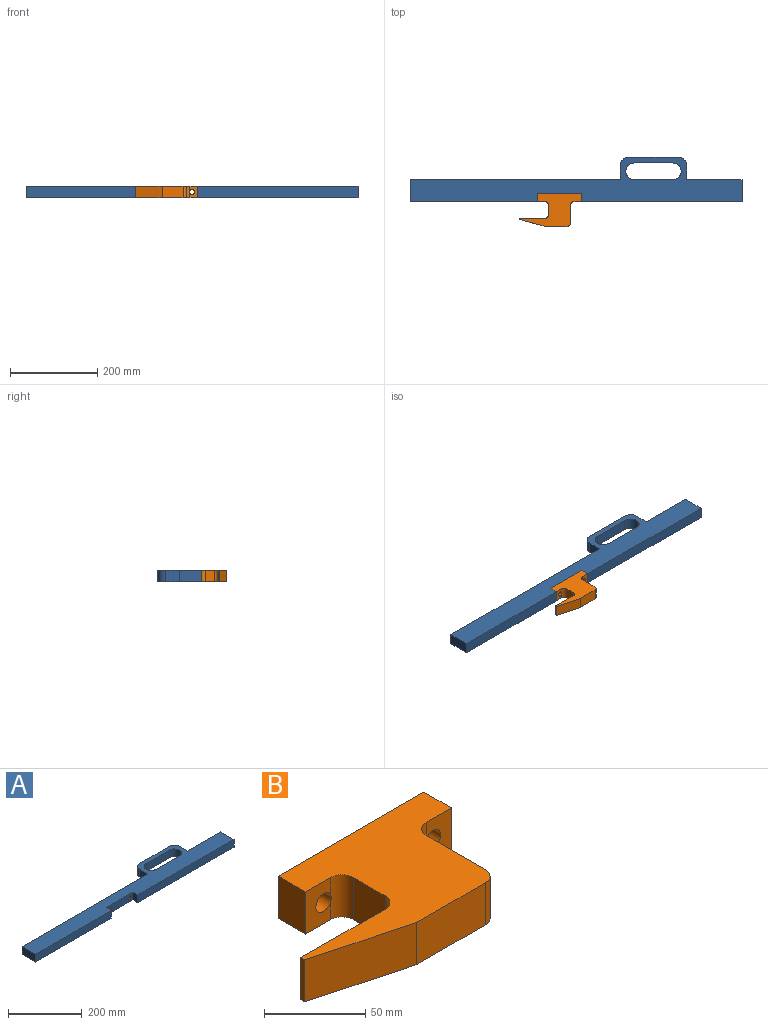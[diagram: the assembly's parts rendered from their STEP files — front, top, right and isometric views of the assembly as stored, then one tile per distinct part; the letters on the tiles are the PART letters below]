
ASSEMBLY  parts=2 mates=1
PART A: 34 faces, bbox 762x101.6x25.4 mm
  f0: plane 368.3x25.4mm, normal (0,-1,0), area 9354.8mm2, adj f1,f7,f14,f28
  f1: plane 762x101.6mm, normal (0,0,1), area 39833.1mm2, adj f0,f4,f5,f6,f7,f8,f9,f10
  f2: cylinder r=6.74mm len=19.05mm, axis (0,1,0), area 807.2mm2, adj f23,f29
  f3: cylinder r=6.74mm len=19.05mm, axis (0,1,0), area 807.2mm2, adj f25,f29
  f4: plane 88.9x25.4mm, normal (0,1,0), area 2258.1mm2, adj f1,f14,f32,f33
  f5: plane 88.9x25.4mm, normal (0,-1,0), area 2258.1mm2, adj f1,f14,f32,f33
  f6: plane 292.1x25.4mm, normal (0,-1,0), area 7419.3mm2, adj f1,f13,f14,f27
  f7: plane 50.8x25.4mm, normal (1,0,0), area 1290.3mm2, adj f0,f1,f8,f14
  f8: plane 127x25.4mm, normal (0,1,0), area 3225.8mm2, adj f1,f7,f9,f14
  f9: plane 31.75x25.4mm, normal (1,0,0), area 806.5mm2, adj f1,f8,f14,f30
  f10: plane 114.3x25.4mm, normal (0,1,0), area 2903.2mm2, adj f1,f14,f30,f31
  f11: plane 31.75x25.4mm, normal (-1,0,0), area 806.5mm2, adj f1,f12,f14,f31
  f12: plane 482.6x25.4mm, normal (0,1,0), area 11017.1mm2, adj f1,f11,f13,f14,f16,f18,f20,f22
  f13: plane 50.8x25.4mm, normal (-1,0,0), area 1290.3mm2, adj f1,f6,f12,f14
  f14: plane 762x101.6mm, normal (0,0,-1), area 39833.1mm2, adj f0,f4,f5,f6,f7,f8,f9,f10
  f15: cone r=0mm half-angle=59deg, axis (0,1,0), area 166.8mm2, adj f16
  f16: cylinder r=6.75mm len=25.98mm, axis (0,1,0), area 1101.1mm2, adj f12,f15
  f17: cone r=0mm half-angle=59deg, axis (0,1,0), area 166.8mm2, adj f18
  f18: cylinder r=6.75mm len=25.98mm, axis (0,1,0), area 1101.1mm2, adj f12,f17
  f19: cone r=0mm half-angle=59deg, axis (0,1,0), area 166.8mm2, adj f20
  f20: cylinder r=6.75mm len=25.98mm, axis (0,1,0), area 1101.1mm2, adj f12,f19
  f21: cone r=0mm half-angle=59deg, axis (0,1,0), area 166.8mm2, adj f22
  f22: cylinder r=6.75mm len=25.98mm, axis (0,1,0), area 1101.1mm2, adj f12,f21
  f23: plane 20.64x20.64mm, normal (0,1,0), area 191.6mm2, adj f2,f24
  f24: cylinder r=10.32mm len=20.64mm, axis (0,1,0), area 823.4mm2, adj f12,f23
  f25: plane 20.64x20.64mm, normal (0,1,0), area 191.6mm2, adj f3,f26
  f26: cylinder r=10.32mm len=20.64mm, axis (0,1,0), area 823.4mm2, adj f12,f25
  f27: plane 25.4x19.05mm, normal (1,0,0), area 483.9mm2, adj f1,f6,f14,f29
  f28: plane 25.4x19.05mm, normal (-1,0,0), area 483.9mm2, adj f0,f1,f14,f29
  f29: plane 101.6x25.4mm, normal (0,-1,0), area 2294.9mm2, adj f1,f2,f3,f14,f27,f28
  f30: cylinder r=19.05mm len=25.4mm, axis (0,0,-1), area 760.1mm2, adj f1,f9,f10,f14
  f31: cylinder r=19.05mm len=25.4mm, axis (0,0,1), area 760.1mm2, adj f1,f10,f11,f14
  f32: cylinder r=19.05mm len=38.1mm, axis (0,0,-1), area 1520.1mm2, adj f1,f4,f5,f14
  f33: cylinder r=19.05mm len=38.1mm, axis (0,0,-1), area 1520.1mm2, adj f1,f4,f5,f14
PART B: 19 faces, bbox 142.8x76.2x25.4 mm
  f0: cylinder r=7.94mm len=25.4mm, axis (0,0,-1), area 314.7mm2, adj f9,f10,f13,f14,f18
  f1: cylinder r=7.94mm len=25.4mm, axis (0,0,1), area 314.7mm2, adj f3,f4,f13,f14,f17
  f2: plane 25.4x19.05mm, normal (-1,0,0), area 483.9mm2, adj f3,f12,f13,f14
  f3: plane 25.41x17.47mm, normal (0,-1,0), area 355.2mm2, adj f1,f2,f13,f14,f17
  f4: plane 25.4x22.23mm, normal (-1,0,0), area 564.5mm2, adj f1,f13,f14,f15
  f5: plane 58.66x25.4mm, normal (0,1,0), area 1489.8mm2, adj f6,f13,f14,f15
  f6: plane 25.4x2.57mm, normal (-1,0,0), area 65.4mm2, adj f5,f7,f13,f14
  f7: plane 61.49x25.4mm, normal (-0.26,-0.97,0), area 1616.9mm2, adj f6,f8,f13,f14
  f8: plane 47.97x25.4mm, normal (0,-1,0), area 1218.4mm2, adj f7,f13,f14,f16
  f9: plane 41.28x25.4mm, normal (1,0,0), area 1048.4mm2, adj f0,f13,f14,f16
  f10: plane 25.41x17.47mm, normal (0,-1,0), area 355.3mm2, adj f0,f11,f13,f14,f18
  f11: plane 25.4x19.05mm, normal (1,0,0), area 483.9mm2, adj f10,f12,f13,f14
  f12: plane 101.6x25.4mm, normal (0,1,0), area 2400.3mm2, adj f2,f11,f13,f14,f17,f18
  f13: plane 142.79x76.2mm, normal (0,0,1), area 5627.8mm2, adj f0,f1,f2,f3,f4,f5,f6,f7
  f14: plane 142.79x76.2mm, normal (0,0,-1), area 5627.8mm2, adj f0,f1,f2,f3,f4,f5,f6,f7
  f15: cylinder r=7.94mm len=25.4mm, axis (0,0,1), area 316.7mm2, adj f4,f5,f13,f14
  f16: cylinder r=7.94mm len=25.4mm, axis (0,0,1), area 316.7mm2, adj f8,f9,f13,f14
  f17: cylinder r=5.36mm len=19.05mm, axis (0,-1,0), area 641.3mm2, adj f1,f3,f12
  f18: cylinder r=5.36mm len=19.05mm, axis (0,-1,0), area 641.3mm2, adj f0,f10,f12
PLACE A t=(-330.34,-16.26,0)mm
PLACE B t=(-330.2,6.35,0)mm
MATE fastened A.f2 <-> B.f17  axis (0,1,0) through (-787.54,2.79,12.7)mm
